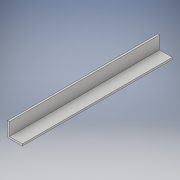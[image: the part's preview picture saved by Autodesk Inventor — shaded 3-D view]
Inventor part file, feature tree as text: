
AUTODESK INVENTOR PART (.ipt)
format: ipt  version: 2017 (Build 210142000, 142)  size: 97,792 bytes
history: native  units: in
note: dims shown in document units (in); Inventor stores cm internally (conversion verified against a paired STEP export)
features: extrude x1, sketch x1
ambient origin geometry x8: Origin, YZ Plane, XZ Plane, XY Plane, X Axis, Y Axis, Z Axis, Center Point
bodies: Solid1 (feature_tree)
feature tree (2):
  extrude  "Extrusion1"  Depth=1.0in
  sketch  "Sketch1"  dims[d4=10.188in d5=0.0in d6=1.0in d7=1.0in]
